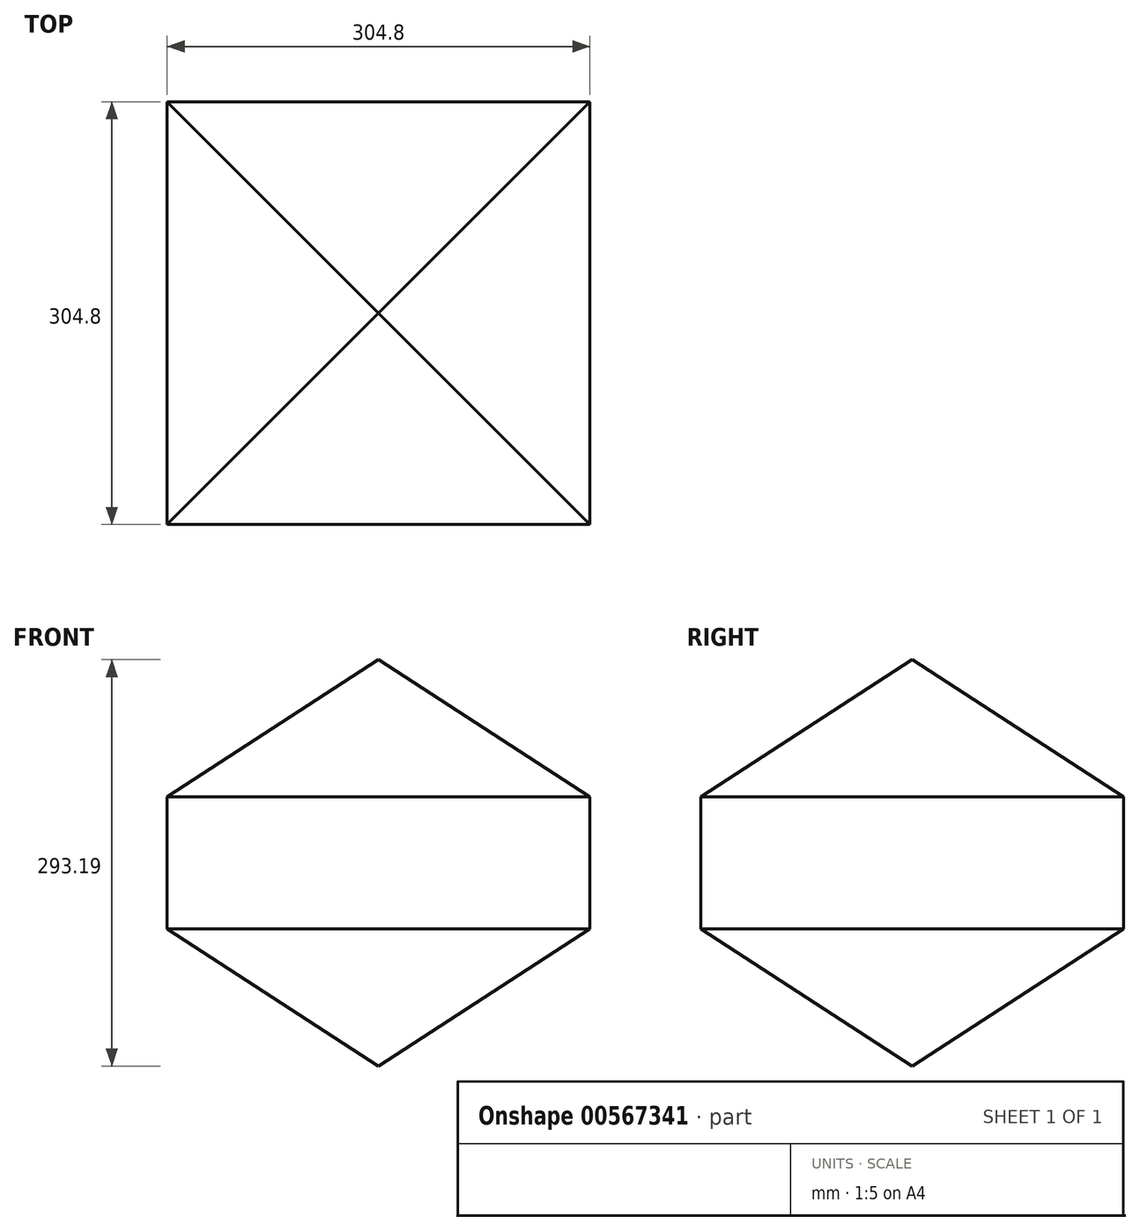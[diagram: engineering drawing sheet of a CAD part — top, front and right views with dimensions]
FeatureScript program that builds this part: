
annotation { "Feature Type Name" : "Feature", "Feature Type Description" : "" }
export const myFeature = defineFeature(function(context is Context, id is Id, definition is map)
    precondition{}
    {
        {
            var Q0;
            Q0=qCreatedBy(makeId("Top.planeOp"),FACE);
            var sketch = newSketch(context, id + "F0", { "sketchPlane" : qUnion([Q0])});
            skLineSegment(sketch, "E0.bottom", {"start": v(0, 0) * mm, "end": v(304.8, 0) * mm});
            skLineSegment(sketch, "E0.top", {"start": v(0, -304.8) * mm, "end": v(304.8, -304.8) * mm});
            skLineSegment(sketch, "E0.left", {"start": v(0, 0) * mm, "end": v(0, -304.8) * mm});
            skLineSegment(sketch, "E0.right", {"start": v(304.8, 0) * mm, "end": v(304.8, -304.8) * mm});
            skSolve(sketch);
        }
        {
            var Q0;
            Q0=makeQuery(id+"F0.imprint","IMPRINT",FACE,{"disambiguationData":[TD([[makeQuery(id+"F0.imprint","IMPRINT",EDGE,{"derivedFrom":sQuery(id+"F0.wireOp",EDGE,"E0.bottom")}),-1.0]])]});
            extrude(context, id + "F1", {"entities" : qUnion([Q0]), "depth" : 95.25 * mm, "offsetDistance" : 25.4 * mm});
        }
        {
            var Q0;
            Q0=makeQuery(id+"F1.opExtrude","CAP_FACE",FACE,{"disambiguationData":[OSD([sQuery(id+"F0.wireOp",EDGE,"E0.bottom"),sQuery(id+"F0.wireOp",EDGE,"E0.top"),sQuery(id+"F0.wireOp",EDGE,"E0.left"),sQuery(id+"F0.wireOp",EDGE,"E0.right")])],"isStart":false});
            extrude(context, id + "F2", {"entities" : qUnion([Q0]), "operationType" : NewBodyOperationType.ADD, "depth" : 101.6 * mm, "offsetDistance" : 25.4 * mm, "hasDraft" : true, "draftAngle" : 57 * degree, "draftPullDirection" : true});
        }
        {
            var Q0;
            Q0=makeQuery(id+"F1.opExtrude","CAP_FACE",FACE,{"disambiguationData":[OSD([sQuery(id+"F0.wireOp",EDGE,"E0.bottom"),sQuery(id+"F0.wireOp",EDGE,"E0.top"),sQuery(id+"F0.wireOp",EDGE,"E0.left"),sQuery(id+"F0.wireOp",EDGE,"E0.right")])],"isStart":true});
            extrude(context, id + "F3", {"entities" : qUnion([Q0]), "operationType" : NewBodyOperationType.ADD, "depth" : 101.6 * mm, "offsetDistance" : 25.4 * mm, "hasDraft" : true, "draftAngle" : 57 * degree, "draftPullDirection" : true});
        }
    });
